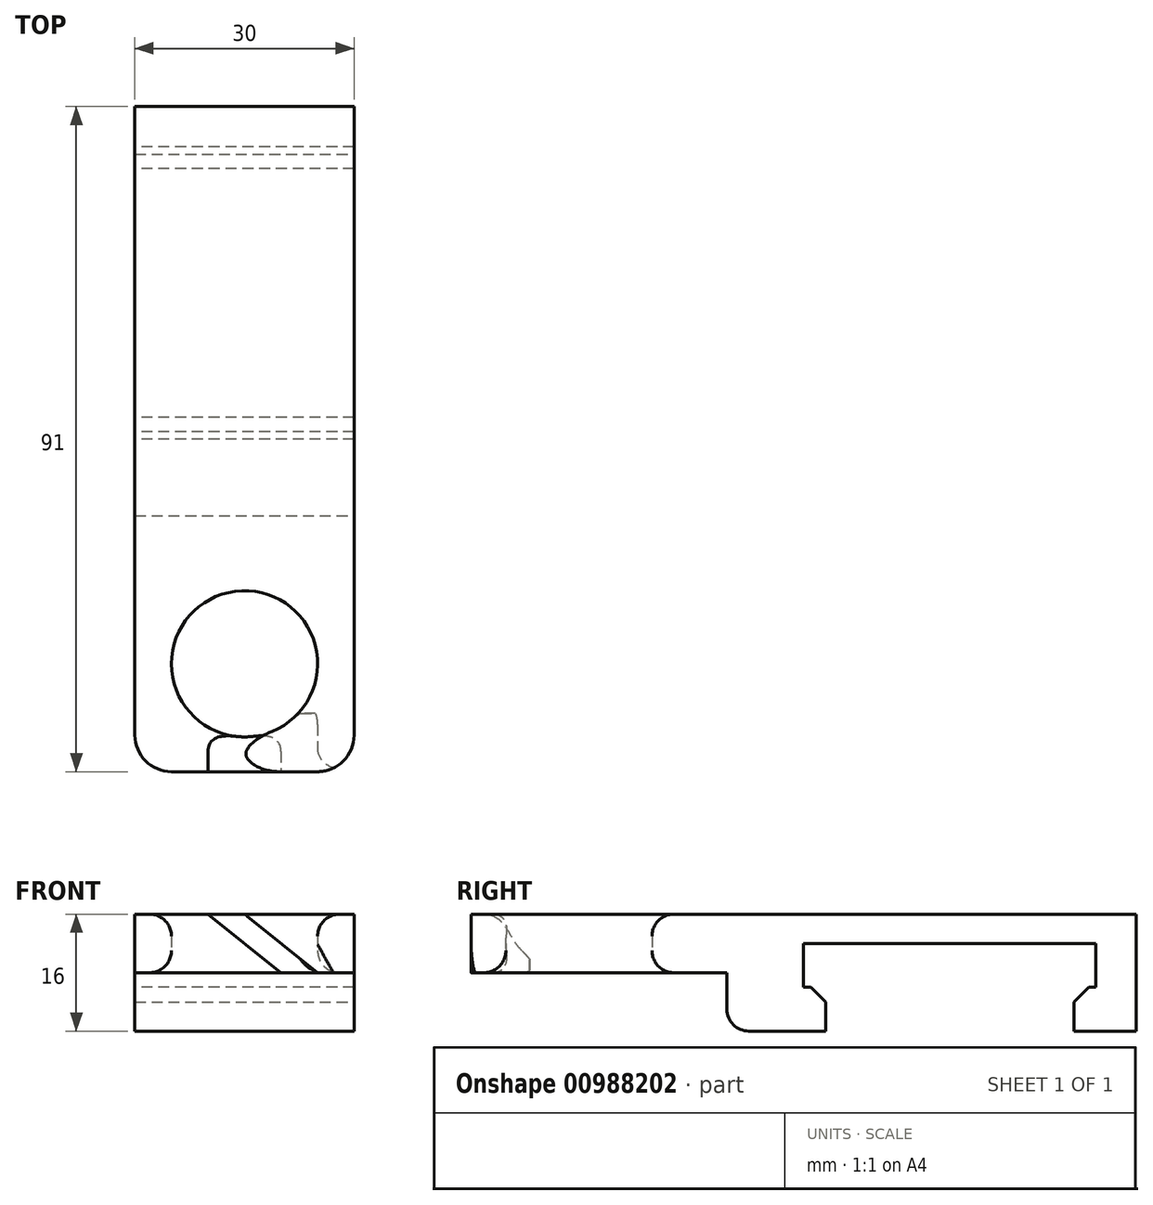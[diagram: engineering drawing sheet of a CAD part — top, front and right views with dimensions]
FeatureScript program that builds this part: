
annotation { "Feature Type Name" : "Feature", "Feature Type Description" : "" }
export const myFeature = defineFeature(function(context is Context, id is Id, definition is map)
    precondition{}
    {
        {
            var Q0;
            Q0=qCreatedBy(makeId("Top.planeOp"),FACE);
            var sketch = newSketch(context, id + "F0", { "sketchPlane" : qUnion([Q0])});
            skLineSegment(sketch, "E0.bottom", {"start": v(15, 45.5) * mm, "end": v(-15, 45.5) * mm});
            skLineSegment(sketch, "E0.top", {"start": v(10, -45.5) * mm, "end": v(-10, -45.5) * mm});
            skLineSegment(sketch, "E0.left", {"start": v(15, 45.5) * mm, "end": v(15, -40.5) * mm});
            skLineSegment(sketch, "E0.right", {"start": v(-15, 45.5) * mm, "end": v(-15, -40.5) * mm});
            skPoint(sketch, "E0.middle", {"position": v(0, 0) * mm});
            skCircle(sketch, "E1", {"center": v(0, -30.74) * mm, "radius": 10 * mm});
            skPoint(sketch, "E2.visualSharp", {"position": v(-15, -45.5) * mm});
            skArc(sketch, "E2.filletArc", {"start": v(-15, -40.5) * mm, "mid": v(-13.54, -44.04) * mm, "end": v(-10, -45.5) * mm});
            skPoint(sketch, "E3.visualSharp", {"position": v(15, -45.5) * mm});
            skArc(sketch, "E3.filletArc", {"start": v(10, -45.5) * mm, "mid": v(13.54, -44.04) * mm, "end": v(15, -40.5) * mm});
            skLineSegment(sketch, "E4", {"start": v(-15, -10.5) * mm, "end": v(15, -10.5) * mm});
            skSolve(sketch);
        }
        {
            var Q0;
            Q0=makeQuery(id+"F0.imprint","IMPRINT",FACE,{"disambiguationData":[TD([[makeQuery(id+"F0.imprint","IMPRINT",EDGE,{"derivedFrom":sQuery(id+"F0.wireOp",EDGE,"E0.bottom")}),1.0]])]});
            extrude(context, id + "F1", {"entities" : qUnion([Q0]), "depth" : 15 * mm, "offsetDistance" : 25 * mm, "hasSecondDirection" : true, "secondDirectionOppositeDirection" : true, "secondDirectionDepth" : 1 * mm});
        }
        {
            var Q0;
            Q0=makeQuery(id+"F0.imprint","IMPRINT",FACE,{"disambiguationData":[TD([[makeQuery(id+"F0.imprint","IMPRINT",EDGE,{"derivedFrom":sQuery(id+"F0.wireOp",EDGE,"E0.top")}),-1.0]])]});
            extrude(context, id + "F2", {"entities" : qUnion([Q0]), "operationType" : NewBodyOperationType.ADD, "depth" : 15 * mm, "offsetDistance" : 25 * mm, "hasSecondDirection" : true, "secondDirectionOppositeDirection" : false, "secondDirectionDepth" : 7 * mm});
        }
        {
            var Q0;
            Q0=makeQuery(id+"F2.opExtrude","CAP_EDGE",EDGE,{"disambiguationData":[OSD([sQuery(id+"F0.wireOp",EDGE,"E4")])],"isStart":true});
            var Q1;
            Q1=makeQuery(id+"F1.opExtrude","CAP_EDGE",EDGE,{"disambiguationData":[OSD([sQuery(id+"F0.wireOp",EDGE,"E4")])],"isStart":true});
            fillet(context, id + "F3", {"entities" : qUnion([Q0, Q1]), "radius" : 3 * mm, "tangentPropagation" : true, "allowEdgeOverflow" : false});
        }
        {
            var Q0;
            Q0=makeQuery(id+"F2.opExtrude","CAP_EDGE",EDGE,{"disambiguationData":[OSD([sQuery(id+"F0.wireOp",EDGE,"E1")])],"isStart":false});
            var Q1;
            Q1=makeQuery(id+"F2.opExtrude","CAP_EDGE",EDGE,{"disambiguationData":[OSD([sQuery(id+"F0.wireOp",EDGE,"E1")])],"isStart":true});
            fillet(context, id + "F4", {"entities" : qUnion([Q0, Q1]), "radius" : 3 * mm, "tangentPropagation" : true, "allowEdgeOverflow" : false});
        }
        {
            var Q0;
            Q0=makeQuery(id+"F2.opExtrude","SWEPT_FACE",FACE,{"disambiguationData":[OSD([sQuery(id+"F0.wireOp",EDGE,"E0.top")])]});
            var sketch = newSketch(context, id + "F5", { "sketchPlane" : qUnion([Q0])});
            skLineSegment(sketch, "E5", {"start": v(0, 15) * mm, "end": v(10, 7) * mm});
            skLineSegment(sketch, "E6", {"start": v(0, 15) * mm, "end": v(-5, 15) * mm, "construction": true});
            skLineSegment(sketch, "E7", {"start": v(-5, 15) * mm, "end": v(5, 7) * mm});
            skSolve(sketch);
        }
        {
            var Q0;
            Q0 = qSketchRegion(id + "F5", true);
            var Q1;
            {var subQ0=sQuery(id+"F5.wireOp",EDGE,"E5");Q1=makeQuery(id+"F5.imprint","IMPRINT",FACE,{"disambiguationData":[TD([[makeQuery(id+"F5.imprint","IMPRINT",EDGE,{"derivedFrom":subQ0}),-1.0]])]});}
            extrude(context, id + "F6", {"entities" : qUnion([Q0, Q1]), "operationType" : NewBodyOperationType.REMOVE, "oppositeDirection" : true, "depth" : 8 * mm, "offsetDistance" : 25 * mm});
        }
        {
            var Q0;
            Q0=makeQuery(id+"F6.boolean.opBoolean","COPY",EDGE,{"derivedFrom":makeQuery(id+"F6.opExtrude","CAP_EDGE",EDGE,{"disambiguationData":[OSD([sQuery(id+"F5.wireOp",EDGE,"E7")])],"isStart":true})});
            var Q1;
            Q1=makeQuery(id+"F6.boolean.opBoolean","COPY",EDGE,{"derivedFrom":makeQuery(id+"F6.opExtrude","CAP_EDGE",EDGE,{"disambiguationData":[OSD([sQuery(id+"F5.wireOp",EDGE,"E5")])],"isStart":true})});
            fillet(context, id + "F7", {"entities" : qUnion([Q0, Q1]), "radius" : 3 * mm, "tangentPropagation" : true, "allowEdgeOverflow" : false});
        }
        {
            var Q0;
            {var subQ0=sQuery(id+"F0.wireOp",EDGE,"E0.right");Q0=makeQuery(id+"F2.boolean.opBoolean","MERGE",FACE,{"derivedFrom":[makeQuery(id+"F1.opExtrude","SWEPT_FACE",FACE,{"disambiguationData":[OSD([subQ0])]}),makeQuery(id+"F2.opExtrude","SWEPT_FACE",FACE,{"disambiguationData":[OSD([subQ0])]})]});}
            var sketch = newSketch(context, id + "F8", { "sketchPlane" : qUnion([Q0])});
            skLineSegment(sketch, "E8", {"start": v(-45.5, 7) * mm, "end": v(-0.5, 7) * mm, "construction": true});
            skLineSegment(sketch, "E9.right", {"start": v(0, 11) * mm, "end": v(0, 5) * mm});
            skLineSegment(sketch, "E10", {"start": v(-40, 11) * mm, "end": v(-40, 10) * mm});
            skLineSegment(sketch, "E11", {"start": v(-40, 11) * mm, "end": v(-40, 5) * mm});
            skLineSegment(sketch, "E12", {"start": v(-40, 5) * mm, "end": v(-37, 5) * mm});
            skLineSegment(sketch, "E13", {"start": v(-40, 11) * mm, "end": v(0, 11) * mm});
            skLineSegment(sketch, "E14", {"start": v(0, 5) * mm, "end": v(-3, 5) * mm});
            skLineSegment(sketch, "E15", {"start": v(-37, 5) * mm, "end": v(-37, -1) * mm});
            skLineSegment(sketch, "E16", {"start": v(-3, 5) * mm, "end": v(-3, -1) * mm});
            skSolve(sketch);
        }
        {
            var Q0;
            {var subQ3=sQuery(id+"F8.wireOp",EDGE,"E9.right");Q0=makeQuery(id+"F8.imprint","IMPRINT",FACE,{"disambiguationData":[TD([[makeQuery(id+"F8.imprint","IMPRINT",EDGE,{"derivedFrom":subQ3}),-1.0]])]});}
            extrude(context, id + "F9", {"entities" : qUnion([Q0]), "operationType" : NewBodyOperationType.REMOVE, "endBound" : BoundingType.UP_TO_NEXT, "oppositeDirection" : true, "depth" : 25 * mm, "offsetDistance" : 25 * mm});
        }
        {
            var Q0;
            Q0=makeQuery(id+"F9.boolean.opBoolean","COPY",EDGE,{"derivedFrom":makeQuery(id+"F9.opExtrude","SWEPT_EDGE",EDGE,{"disambiguationData":[OSD([sQuery(id+"F8.wireOp",EDGE,"E12"),sQuery(id+"F8.wireOp",EDGE,"E15")])]})});
            var Q1;
            Q1=makeQuery(id+"F9.boolean.opBoolean","COPY",EDGE,{"derivedFrom":makeQuery(id+"F9.opExtrude","SWEPT_EDGE",EDGE,{"disambiguationData":[OSD([sQuery(id+"F8.wireOp",EDGE,"E14"),sQuery(id+"F8.wireOp",EDGE,"E16")])]})});
            chamfer(context, id + "F10", {"entities" : qUnion([Q0, Q1]), "width" : 2 * mm, "tangentPropagation" : true});
        }
    });
